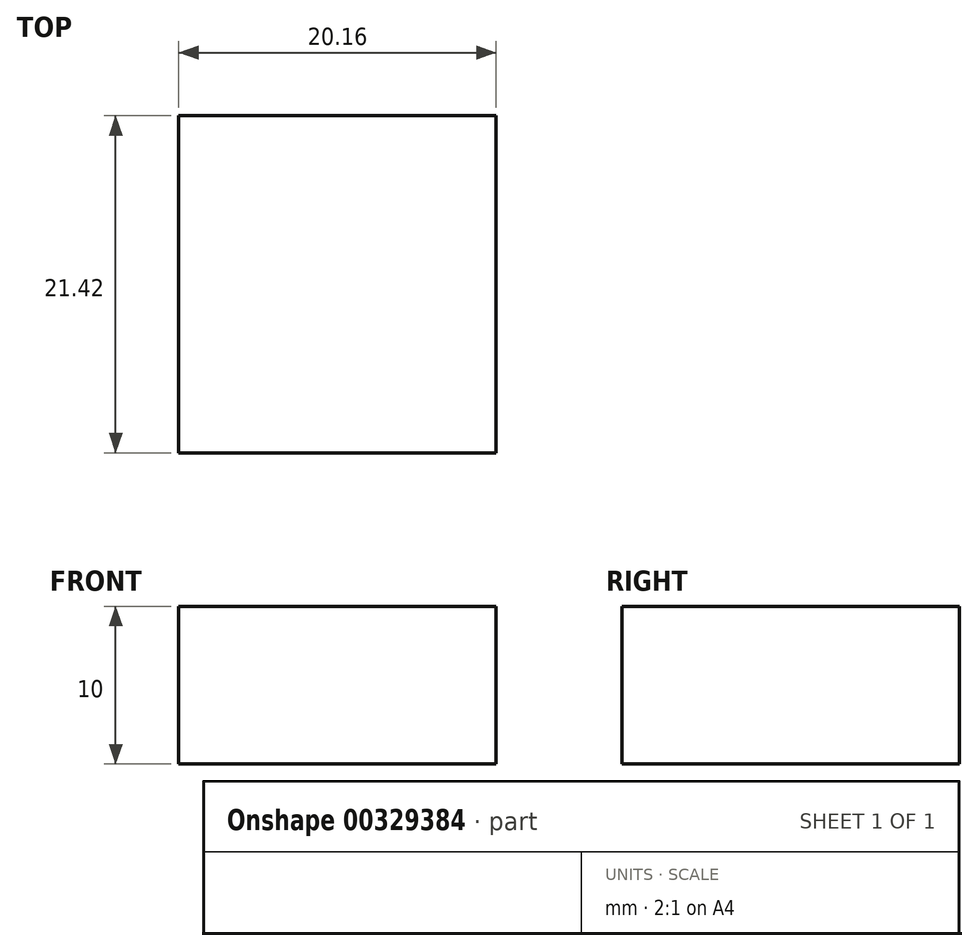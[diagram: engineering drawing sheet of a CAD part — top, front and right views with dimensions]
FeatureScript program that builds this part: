
annotation { "Feature Type Name" : "Feature", "Feature Type Description" : "" }
export const myFeature = defineFeature(function(context is Context, id is Id, definition is map)
    precondition{}
    {
        {
            var Q0;
            Q0=qCreatedBy(makeId("Top.planeOp"),FACE);
            var sketch = newSketch(context, id + "F0", { "sketchPlane" : qUnion([Q0])});
            skLineSegment(sketch, "E0.bottom", {"start": v(10.7, -10.08) * mm, "end": v(-9.45, -10.08) * mm});
            skLineSegment(sketch, "E0.top", {"start": v(10.7, 11.34) * mm, "end": v(-9.45, 11.34) * mm});
            skLineSegment(sketch, "E0.left", {"start": v(10.7, -10.08) * mm, "end": v(10.7, 11.34) * mm});
            skLineSegment(sketch, "E0.right", {"start": v(-9.45, -10.08) * mm, "end": v(-9.45, 11.34) * mm});
            skPoint(sketch, "E0.middle", {"position": v(0.63, 0.63) * mm});
            skSolve(sketch);
        }
        {
            var Q0;
            Q0=makeQuery(id+"F0.imprint","IMPRINT",FACE,{"disambiguationData":[TD([[makeQuery(id+"F0.imprint","IMPRINT",EDGE,{"derivedFrom":sQuery(id+"F0.wireOp",EDGE,"E0.bottom")}),-1.0]])]});
            extrude(context, id + "F1", {"entities" : qUnion([Q0]), "depth" : 10 * mm});
        }
    });
